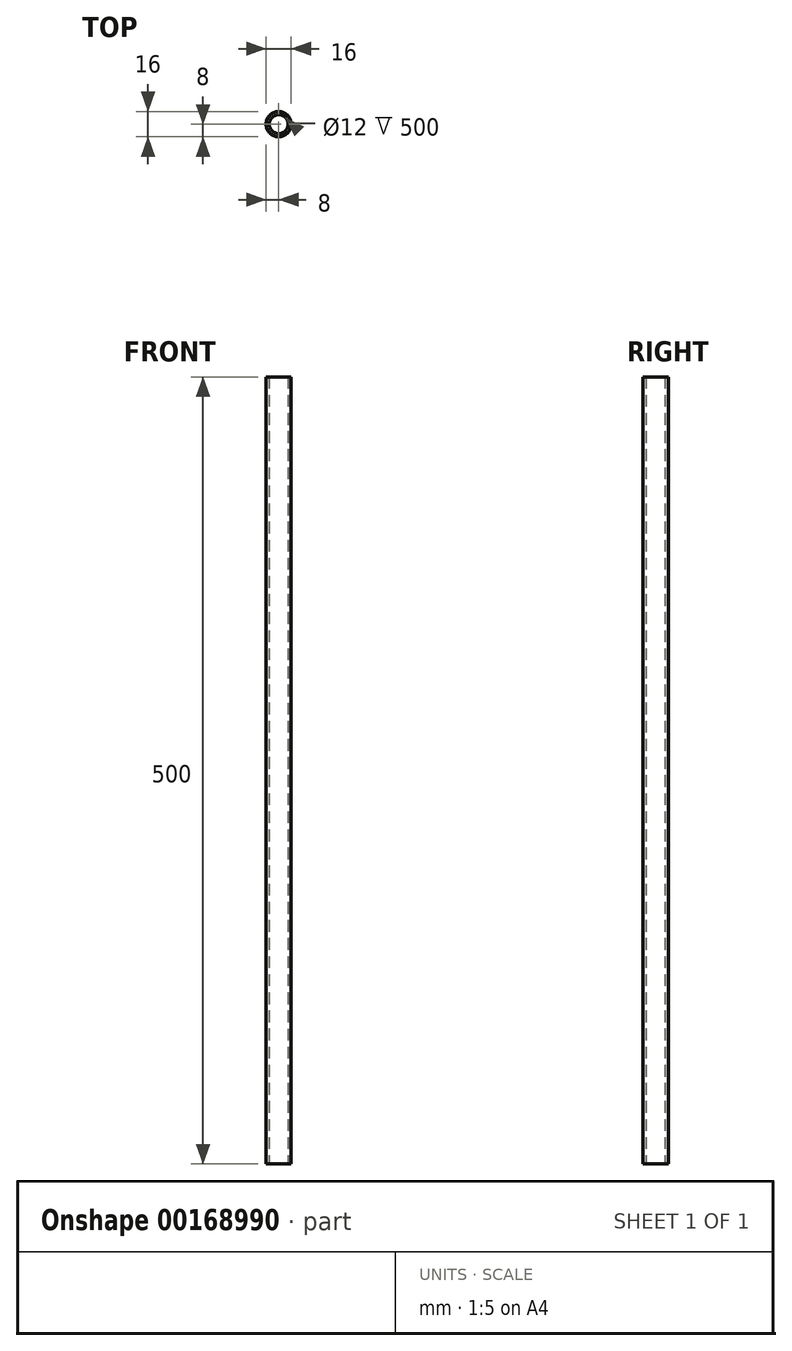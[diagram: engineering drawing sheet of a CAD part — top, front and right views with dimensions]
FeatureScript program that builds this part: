
annotation { "Feature Type Name" : "Feature", "Feature Type Description" : "" }
export const myFeature = defineFeature(function(context is Context, id is Id, definition is map)
    precondition{}
    {
        {
            var Q0;
            Q0=qCreatedBy(makeId("Top.planeOp"),FACE);
            var sketch = newSketch(context, id + "F0", { "sketchPlane" : qUnion([Q0])});
            skCircle(sketch, "E0", {"center": v(0, 0) * mm, "radius": 6 * mm});
            skCircle(sketch, "E1", {"center": v(0, 0) * mm, "radius": 8 * mm});
            skSolve(sketch);
        }
        {
            var Q0;
            Q0=makeQuery(id+"F0.imprint","IMPRINT",FACE,{"disambiguationData":[TD([[makeQuery(id+"F0.imprint","IMPRINT",EDGE,{"derivedFrom":sQuery(id+"F0.wireOp",EDGE,"E0")}),-1.0]])]});
            extrude(context, id + "F1", {"entities" : qUnion([Q0]), "depth" : 500 * mm});
        }
    });
